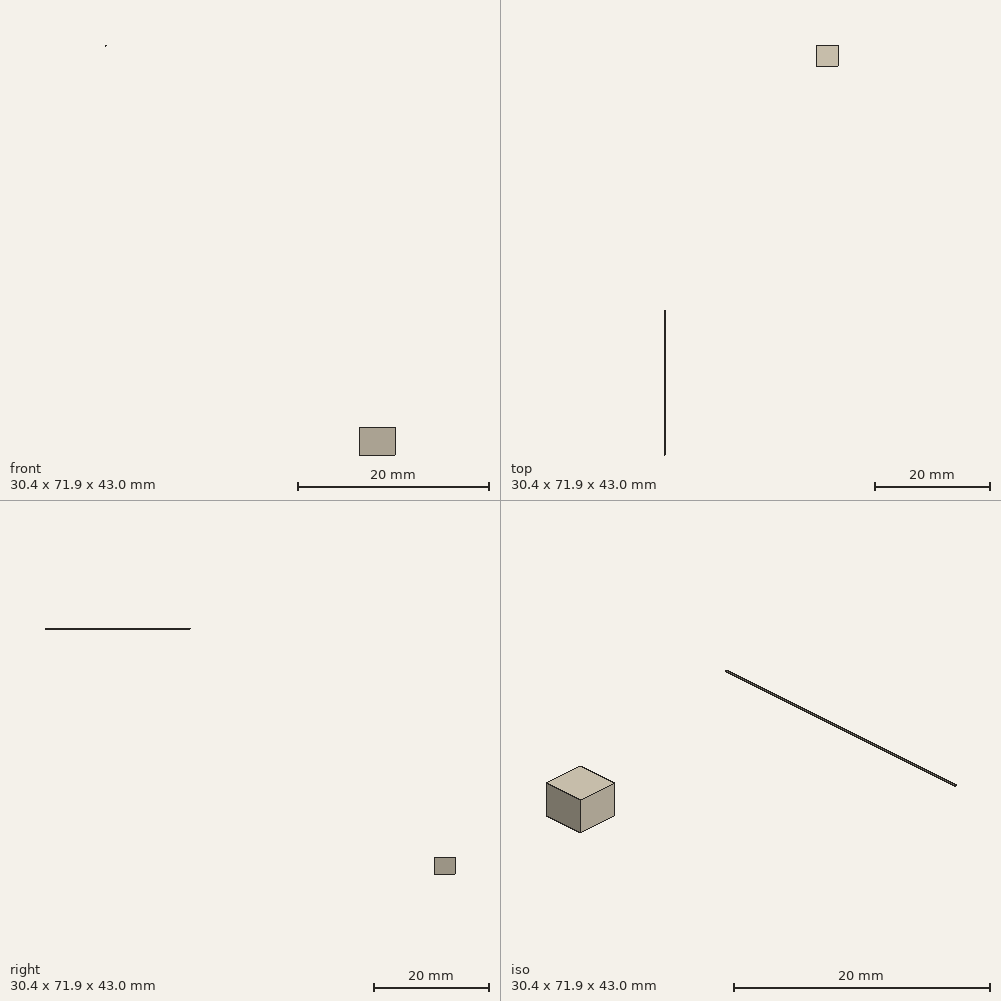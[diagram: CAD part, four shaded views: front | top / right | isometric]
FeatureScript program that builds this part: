
annotation { "Feature Type Name" : "Feature", "Feature Type Description" : "" }
export const myFeature = defineFeature(function(context is Context, id is Id, definition is map)
    precondition{}
    {
        {
            var Q0;
            Q0=qCreatedBy(makeId("Front.planeOp"),FACE);
            var sketch = newSketch(context, id + "F0", { "sketchPlane" : qUnion([Q0])});
            skCircle(sketch, "E0", {"center": v(-47.33, 42.94) * mm, "radius": 0.06 * mm});
            skSolve(sketch);
        }
        {
            var Q0;
            Q0=makeQuery(id+"F0.imprint","IMPRINT",FACE,{"disambiguationData":[TD([[makeQuery(id+"F0.imprint","IMPRINT",EDGE,{"derivedFrom":sQuery(id+"F0.wireOp",EDGE,"E0")}),1.0]])]});
            extrude(context, id + "F1", {"entities" : qUnion([Q0]), "depth" : 25.4 * mm});
        }
        {
            var Q0;
            Q0=qCreatedBy(makeId("Top.planeOp"),FACE);
            var sketch = newSketch(context, id + "F2", { "sketchPlane" : qUnion([Q0])});
            skLineSegment(sketch, "E1.bottom", {"start": v(-20.7, 46.5) * mm, "end": v(-16.94, 46.5) * mm});
            skLineSegment(sketch, "E1.top", {"start": v(-20.7, 42.73) * mm, "end": v(-16.94, 42.73) * mm});
            skLineSegment(sketch, "E1.left", {"start": v(-20.7, 46.5) * mm, "end": v(-20.7, 42.73) * mm});
            skLineSegment(sketch, "E1.right", {"start": v(-16.94, 46.5) * mm, "end": v(-16.94, 42.73) * mm});
            skSolve(sketch);
        }
        {
            var Q0;
            Q0=makeQuery(id+"F2.imprint","IMPRINT",FACE,{"disambiguationData":[TD([[makeQuery(id+"F2.imprint","IMPRINT",EDGE,{"derivedFrom":sQuery(id+"F2.wireOp",EDGE,"E1.bottom")}),-1.0]])]});
            extrude(context, id + "F3", {"entities" : qUnion([Q0]), "depth" : 2.95 * mm});
        }
    });
